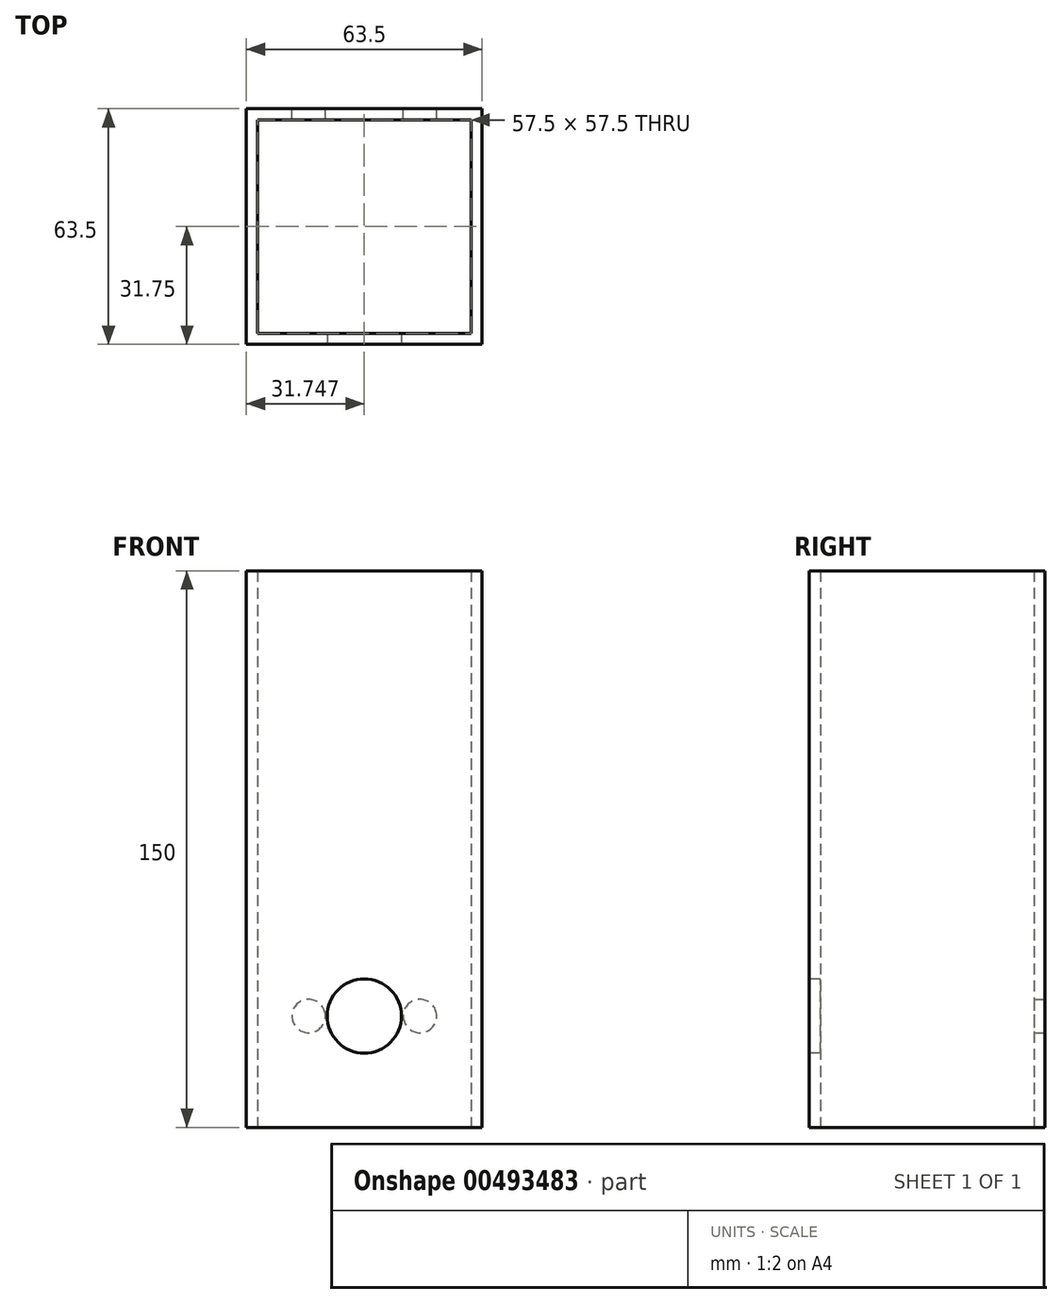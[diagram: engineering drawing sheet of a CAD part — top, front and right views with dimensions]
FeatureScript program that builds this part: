
annotation { "Feature Type Name" : "Feature", "Feature Type Description" : "" }
export const myFeature = defineFeature(function(context is Context, id is Id, definition is map)
    precondition{}
    {
        {
            var Q0;
            Q0=qCreatedBy(makeId("Top.planeOp"),FACE);
            var sketch = newSketch(context, id + "F0", { "sketchPlane" : qUnion([Q0])});
            skLineSegment(sketch, "E0.bottom", {"start": v(-26.31, 30.47) * mm, "end": v(31.19, 30.47) * mm});
            skLineSegment(sketch, "E0.top", {"start": v(-26.31, -27.03) * mm, "end": v(31.19, -27.03) * mm});
            skLineSegment(sketch, "E0.left", {"start": v(-26.31, 30.47) * mm, "end": v(-26.31, -27.03) * mm});
            skLineSegment(sketch, "E0.right", {"start": v(31.19, 30.47) * mm, "end": v(31.19, -27.03) * mm});
            skLineSegment(sketch, "E1.bottom", {"start": v(-29.31, 33.47) * mm, "end": v(34.19, 33.47) * mm});
            skLineSegment(sketch, "E1.top", {"start": v(-29.31, -30.03) * mm, "end": v(34.19, -30.03) * mm});
            skLineSegment(sketch, "E1.left", {"start": v(-29.31, 33.47) * mm, "end": v(-29.31, -30.03) * mm});
            skLineSegment(sketch, "E1.right", {"start": v(34.19, 33.47) * mm, "end": v(34.19, -30.03) * mm});
            skSolve(sketch);
        }
        {
            var Q0;
            Q0 = qSketchRegion(id + "F0", true);
            extrude(context, id + "F1", {"entities" : qUnion([Q0]), "flatOperationType" : FlatOperationType.REMOVE, "offsetDistance" : 25 * mm, "depth" : 150 * mm, "domain" : OperationDomain.MODEL});
        }
        {
            var Q0;
            Q0=makeQuery(id+"F1.opExtrude","SWEPT_FACE",FACE,{"disambiguationData":[OSD([sQuery(id+"F0.wireOp",EDGE,"E1.top")])]});
            var sketch = newSketch(context, id + "F2", { "sketchPlane" : qUnion([Q0])});
            skCircle(sketch, "E2", {"center": v(2.44, 30) * mm, "radius": 10 * mm});
            skSolve(sketch);
        }
        {
            var Q0;
            Q0 = qSketchRegion(id + "F2", true);
            extrude(context, id + "F3", {"entities" : qUnion([Q0]), "operationType" : NewBodyOperationType.REMOVE, "oppositeDirection" : true, "depth" : 3 * mm, "offsetDistance" : 25 * mm});
        }
        {
            var Q0;
            Q0=makeQuery(id+"F1.opExtrude","SWEPT_FACE",FACE,{"disambiguationData":[OSD([sQuery(id+"F0.wireOp",EDGE,"E1.bottom")])]});
            var sketch = newSketch(context, id + "F4", { "sketchPlane" : qUnion([Q0])});
            skCircle(sketch, "E3", {"center": v(-17.44, 30) * mm, "radius": 4.5 * mm});
            skCircle(sketch, "E4", {"center": v(12.56, 30) * mm, "radius": 4.5 * mm});
            skSolve(sketch);
        }
        {
            var Q0;
            Q0 = qSketchRegion(id + "F4", true);
            extrude(context, id + "F5", {"entities" : qUnion([Q0]), "operationType" : NewBodyOperationType.REMOVE, "oppositeDirection" : true, "depth" : 3 * mm, "offsetDistance" : 25 * mm});
        }
    });
